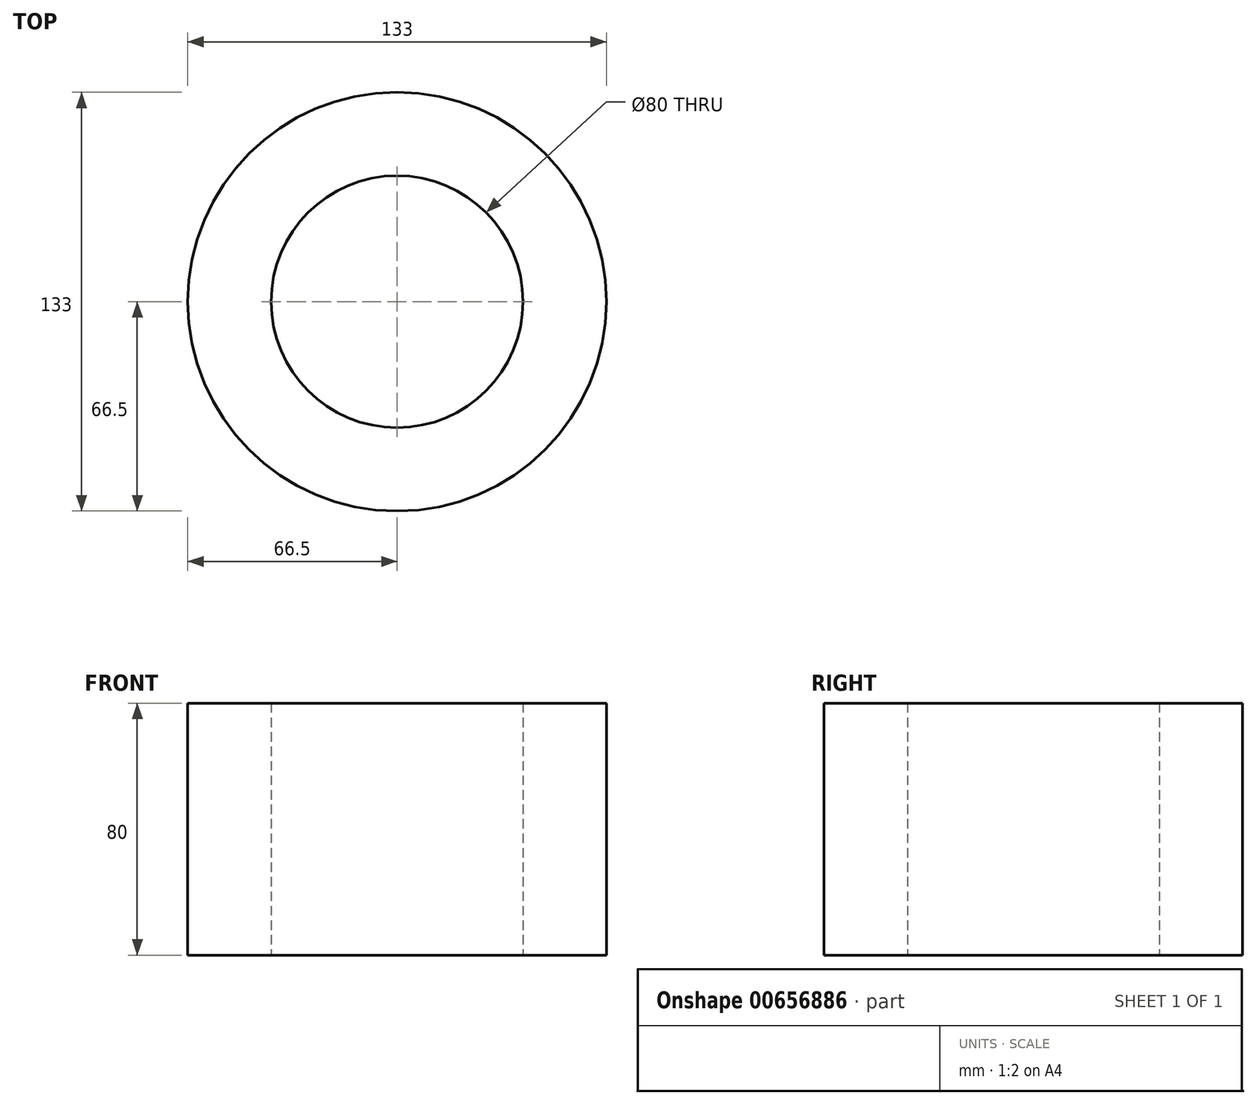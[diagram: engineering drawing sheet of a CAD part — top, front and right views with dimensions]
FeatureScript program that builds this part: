
annotation { "Feature Type Name" : "Feature", "Feature Type Description" : "" }
export const myFeature = defineFeature(function(context is Context, id is Id, definition is map)
    precondition{}
    {
        {
            var Q0;
            Q0=qCreatedBy(makeId("Top.planeOp"),FACE);
            var sketch = newSketch(context, id + "F0", { "sketchPlane" : qUnion([Q0])});
            skCircle(sketch, "E0", {"center": v(0, 0) * mm, "radius": 66.5 * mm});
            skCircle(sketch, "E1", {"center": v(0, 0) * mm, "radius": 40 * mm});
            skSolve(sketch);
        }
        {
            var Q0;
            Q0 = qSketchRegion(id + "F0", true);
            extrude(context, id + "F1", {"entities" : qUnion([Q0]), "depth" : 80 * mm, "offsetDistance" : 25 * mm});
        }
        {
            var Q0;
            Q0 = qSketchRegion(id + "F0", true);
            extrude(context, id + "F2", {"entities" : qUnion([Q0]), "operationType" : NewBodyOperationType.ADD, "depth" : 25 * mm, "offsetDistance" : 25 * mm});
        }
    });
